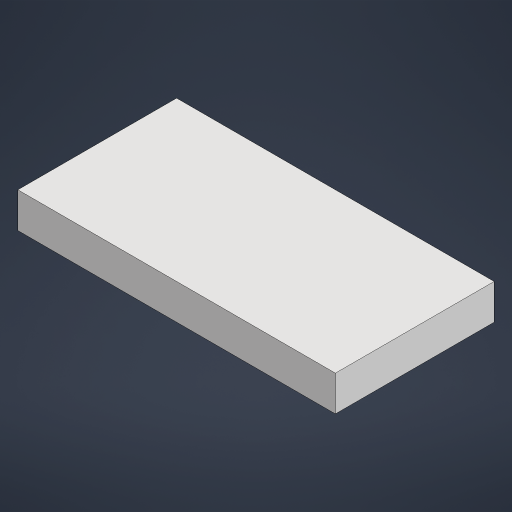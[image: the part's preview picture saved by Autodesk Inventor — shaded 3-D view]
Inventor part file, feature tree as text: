
AUTODESK INVENTOR PART (.ipt)
format: ipt  version: 2023.2 (Build 272271000, 271)  size: 148,480 bytes
history: native  units: in
note: dims shown in document units (in); Inventor stores cm internally (conversion verified against a paired STEP export)
features: extrude x1, sketch x1
ambient origin geometry x8: Origin, YZ Plane, XZ Plane, XY Plane, X Axis, Y Axis, Z Axis, Center Point
bodies: Solid1 (feature_tree)
feature tree (2):
  extrude  "Extrusion1"  Depth=18.0in
  sketch  "Sketch2"  dims[d3=36.0in d4=18.0in d5=4.0in d6=0.0in]
